# Revit family: LOROWERK 21722-070X
name_source: partatom
category: Sanitärinstallationen
revit_build: Autodesk Revit 2017 (Build: 20160225_1515(x64)
units: mm (PartAtom-declared; Revit-internal decimal feet)

## family parameters
Arbeitsebenenbasiert = Nein
Beim Laden mit Abzugskörper schneiden = Nein
Bemaßung runder Anschluss = Durchmesser verwenden
Gemeinsam genutzt = Nein
Immer vertikal = Ja
Raumberechnungspunkt = Nein
Teiletyp = Normal

## types (1)
- LOROWERK 21722-070X
    38.710.01.13 = mittig
    38.710.01.5 = DN
    Abdichtvarianten = mit Klemmflansch
    Abflussstutzen Ausführung = senkrecht
    Ablaufanschluss = 1
    Art der Nenn-/Betriebsspannung = nicht zutreffend
    BIM = https://media.stage.bim.site
    Beschreibung = LORO-DRAINLET DL Flachdachabläufe, zweiteilig
    Bestellmenge (Multiplikator) = 1
    CONNECTOR0_DIAMETER_dZ_0r = 70 mm
    CONNECTOR0_dZ_00 = 47 mm
    CONNECTOR0_dZ_01 = 48 mm
    CONNECTOR0_ref_dZ = 48 mm
    CONNECTOR1_DIAMETER_dZ_0r = 70 mm
    CONNECTOR1_dZ_00 = 260 mm
    CONNECTOR1_dZ_01 = 23 mm
    CONNECTOR1_ref_dZ = 23 mm
    DATANORM = 21722.070X
    Einbaubreite [m] = 0.413
    Einbautiefe [m] = 0.035
    Feuerwiderstandsklasse = keine Feuerwiderstandsklasse
    Feuerwiderstandsklasse nachrüstbar = nein
    GTIN = 4038088073667
    Gehäuseanschlussarten = Ablauf punktförmig
    Geruchsverschluss = ohne Geruchsverschluss
    HAN = 21722.070X
    Heizung = ohne Heizung
    Hersteller = LOROWERK K.H. Vahlbrauk GmbH & Co. KG
    Ist System = Nein
    Ist Zubehör = Nein
    Kommentar = Kompletteinheit Serie 84 zweiteilig
    Nenndruck = 260
    Nenndrucksystem = 260
    Nennweitensystem = PN
    Potenzialausgleich (Erdungsanschluss)   vorhanden = ja
    Produktbezeichnung = LORO-DL Notablauf, Edelstahl, Klemmflansch, senkr., 2-tlg., mit WD, DN70
    Produktklassifikation = Flachdachablauf
    Produktname = LORO-DL Notablauf, Edelstahl, Klemmflansch, senkr., 2-tlg., mit WD, DN70
    Produktvideo = https://media.stage.bim.site
    Sperrwasserhöhe [m] = 0
    Typname = LORO-DL Notablauf, Edelstahl, Klemmflansch, senkr., 2-tlg., mit WD, DN70
    VDIBSN = 0020020000010010000010010010010000000030020000000500000001
    Werkstoff des Ablaufkörpers = nicht rostender Stahl
    Wärmedämmung = mit Wärmedämmung
    elektrischer Anschluss = nein
